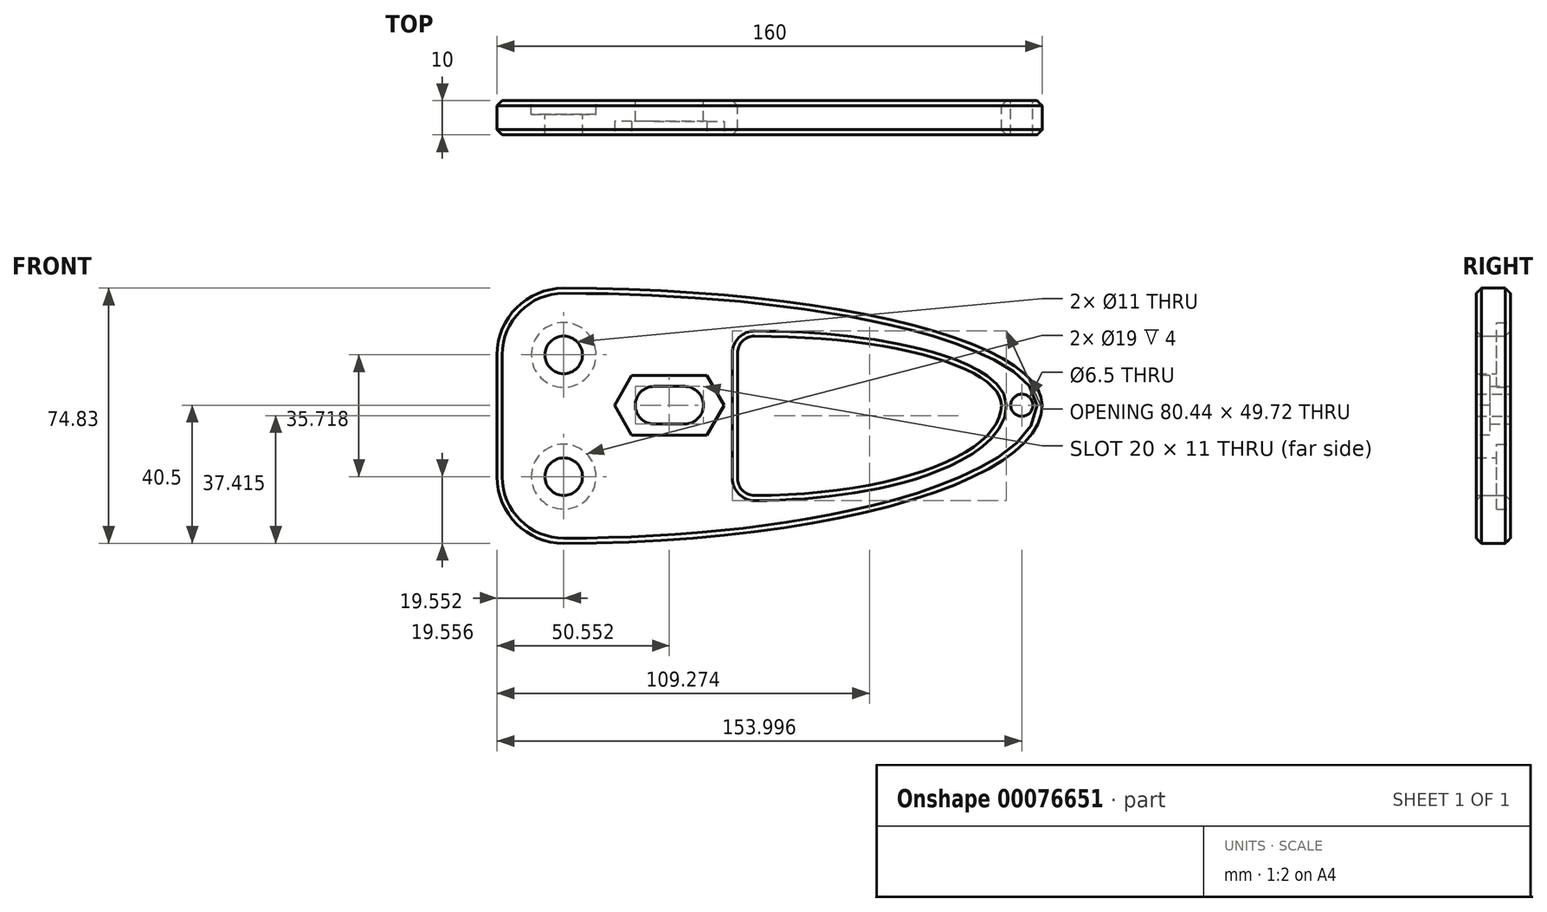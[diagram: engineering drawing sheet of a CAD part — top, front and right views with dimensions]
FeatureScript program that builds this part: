
annotation { "Feature Type Name" : "Feature", "Feature Type Description" : "" }
export const myFeature = defineFeature(function(context is Context, id is Id, definition is map)
    precondition{}
    {
        {
            var Q0;
            Q0=qCreatedBy(makeId("Front.planeOp"),FACE);
            var sketch = newSketch(context, id + "F0", { "sketchPlane" : qUnion([Q0])});
            skArc(sketch, "E0.filletArc", {"start": v(-61.04, 34.33) * mm, "mid": v(-74.87, 28.6) * mm, "end": v(-80.6, 14.77) * mm});
            skArc(sketch, "E1.filletArc", {"start": v(-80.6, -20.94) * mm, "mid": v(-74.87, -34.77) * mm, "end": v(-61.04, -40.5) * mm});
            skCircle(sketch, "E2", {"center": v(-61.04, -20.94) * mm, "radius": 5.5 * mm});
            skCircle(sketch, "E3", {"center": v(-61.04, 14.77) * mm, "radius": 5.5 * mm});
            skArc(sketch, "E4", {"start": v(-25.54, -5.5) * mm, "mid": v(-20.04, 0) * mm, "end": v(-25.54, 5.5) * mm});
            skPoint(sketch, "E5.center.orphan", {"position": v(-61.04, 0) * mm});
            skPoint(sketch, "E6", {"position": v(-80.6, 0) * mm});
            skPoint(sketch, "E7", {"position": v(-10.04, 0) * mm});
            skPoint(sketch, "E8", {"position": v(79.4, 0) * mm});
            skPoint(sketch, "E9", {"position": v(-20.04, 0) * mm});
            skArc(sketch, "E10", {"start": v(-34.54, 5.5) * mm, "mid": v(-40.04, 0) * mm, "end": v(-34.54, -5.5) * mm});
            skLineSegment(sketch, "E11", {"start": v(-34.54, 5.5) * mm, "end": v(-25.54, 5.5) * mm});
            skLineSegment(sketch, "E12", {"start": v(-34.54, -5.5) * mm, "end": v(-25.54, -5.5) * mm});
            skEllipticalArc(sketch, "E13", {});
            skEllipticalArc(sketch, "E14.trimOffspring", {});
            skLineSegment(sketch, "E15", {"start": v(79.4, 0) * mm, "end": v(67.4, 0) * mm});
            skEllipticalArc(sketch, "E16", {});
            skEllipticalArc(sketch, "E17.trimOffspring", {});
            skLineSegment(sketch, "E18", {"start": v(-5.04, 20.27) * mm, "end": v(-5.04, 20.27) * mm});
            skLineSegment(sketch, "E19", {"start": v(-10.04, 15.27) * mm, "end": v(-10.04, 0) * mm});
            skLineSegment(sketch, "E20", {"start": v(-10.04, 0) * mm, "end": v(-10.04, -21.44) * mm});
            skLineSegment(sketch, "E21", {"start": v(-5.04, -26.44) * mm, "end": v(-5.04, -26.44) * mm});
            skPoint(sketch, "E22.start.orphan", {"position": v(-61.04, 20.27) * mm});
            skPoint(sketch, "E23.start.orphan", {"position": v(-61.04, -26.44) * mm});
            skLineSegment(sketch, "E24", {"start": v(-80.6, 14.77) * mm, "end": v(-80.6, -20.94) * mm});
            skPoint(sketch, "E25.visualSharp", {"position": v(-10.04, 20.27) * mm});
            skArc(sketch, "E25.filletArc", {"start": v(-5.04, 20.27) * mm, "mid": v(-8.57, 18.8) * mm, "end": v(-10.04, 15.27) * mm});
            skPoint(sketch, "E26.visualSharp", {"position": v(-10.04, -26.44) * mm});
            skArc(sketch, "E26.filletArc", {"start": v(-10.04, -21.44) * mm, "mid": v(-8.57, -24.98) * mm, "end": v(-5.04, -26.44) * mm});
            skCircle(sketch, "E27", {"center": v(73.4, 0) * mm, "radius": 3.25 * mm});
            skCircle(sketch, "E28", {"center": v(-61.04, 14.77) * mm, "radius": 9.5 * mm});
            skCircle(sketch, "E29", {"center": v(-61.04, -20.94) * mm, "radius": 9.5 * mm});
            const initialGuessF0  = {"E13": [-0.061037882258116044, 0, 0, -1, 0.0405, 0.140444, 6.283185307179586, 1.5707963267948966], "E14.trimOffspring": [-0.061037882258116044, 0, 0, 1, 0.03433, 0.140444, 4.71238898038469, 6.283185307179586], "E16": [-0.005037882258116042, 0, 0, 1, 0.020274, 0.072444, 4.71238898038469, 6.283185307179586], "E17.trimOffspring": [-0.005037882258116042, 0, 0, -1, 0.026444, 0.072444, 6.283185307179586, 1.5707963267948966]};
            skSetInitialGuess(sketch, initialGuessF0);
            skSolve(sketch);
        }
        {
            var Q0;
            Q0 = qSketchRegion(id + "F0", true);
            var Q1;
            Q1=makeQuery(id+"F0.imprint","IMPRINT",FACE,{"disambiguationData":[TD([[makeQuery(id+"F0.imprint","IMPRINT",EDGE,{"derivedFrom":sQuery(id+"F0.wireOp",EDGE,"E3")}),-1.0]])]});
            var Q2;
            Q2=makeQuery(id+"F0.imprint","IMPRINT",FACE,{"disambiguationData":[TD([[makeQuery(id+"F0.imprint","IMPRINT",EDGE,{"derivedFrom":sQuery(id+"F0.wireOp",EDGE,"E2")}),-1.0]])]});
            extrude(context, id + "F1", {"entities" : qUnion([Q0, Q1, Q2]), "depth" : 10 * mm});
        }
        {
            var Q0;
            Q0=makeQuery(id+"F0.imprint","IMPRINT",FACE,{"disambiguationData":[TD([[makeQuery(id+"F0.imprint","IMPRINT",EDGE,{"derivedFrom":sQuery(id+"F0.wireOp",EDGE,"E3")}),-1.0]])]});
            var Q1;
            Q1=makeQuery(id+"F0.imprint","IMPRINT",FACE,{"disambiguationData":[TD([[makeQuery(id+"F0.imprint","IMPRINT",EDGE,{"derivedFrom":sQuery(id+"F0.wireOp",EDGE,"E2")}),-1.0]])]});
            extrude(context, id + "F2", {"entities" : qUnion([Q0, Q1]), "operationType" : NewBodyOperationType.REMOVE, "depth" : 4 * mm});
        }
        {
            var Q0;
            Q0=makeQuery(id+"F1.opExtrude","CAP_FACE",FACE,{"disambiguationData":[OSD([sQuery(id+"F0.wireOp",EDGE,"E0.filletArc"),sQuery(id+"F0.wireOp",EDGE,"E1.filletArc"),sQuery(id+"F0.wireOp",EDGE,"E2"),sQuery(id+"F0.wireOp",EDGE,"E3"),sQuery(id+"F0.wireOp",EDGE,"E4"),sQuery(id+"F0.wireOp",EDGE,"E10"),sQuery(id+"F0.wireOp",EDGE,"E11"),sQuery(id+"F0.wireOp",EDGE,"E12"),sQuery(id+"F0.wireOp",EDGE,"E13"),sQuery(id+"F0.wireOp",EDGE,"E14.trimOffspring"),sQuery(id+"F0.wireOp",EDGE,"E16"),sQuery(id+"F0.wireOp",EDGE,"E17.trimOffspring"),sQuery(id+"F0.wireOp",EDGE,"E19"),sQuery(id+"F0.wireOp",EDGE,"E20"),sQuery(id+"F0.wireOp",EDGE,"E24"),sQuery(id+"F0.wireOp",EDGE,"E25.filletArc"),sQuery(id+"F0.wireOp",EDGE,"E26.filletArc"),sQuery(id+"F0.wireOp",EDGE,"E27")])],"isStart":false});
            var sketch = newSketch(context, id + "F3", { "sketchPlane" : qUnion([Q0])});
            skPoint(sketch, "E30", {"position": v(-20.04, 0) * mm});
            skPoint(sketch, "E31", {"position": v(-29.04, 0) * mm});
            skLineSegment(sketch, "E32.1", {"start": v(-18.99, 8.75) * mm, "end": v(-13.93, 0) * mm});
            skLineSegment(sketch, "E32.2", {"start": v(-13.93, 0) * mm, "end": v(-18.99, -8.75) * mm});
            skLineSegment(sketch, "E33", {"start": v(-18.99, 8.75) * mm, "end": v(-41.09, 8.75) * mm});
            skLineSegment(sketch, "E34", {"start": v(-41.09, -8.75) * mm, "end": v(-18.99, -8.75) * mm});
            skPoint(sketch, "E35", {"position": v(-40.04, 0) * mm});
            skPoint(sketch, "E36", {"position": v(-31.04, 0) * mm});
            skLineSegment(sketch, "E37", {"start": v(-40.04, 0) * mm, "end": v(-20.04, 0) * mm});
            skLineSegment(sketch, "E38", {"start": v(-30.04, 0) * mm, "end": v(-30.04, 8.75) * mm, "construction": true});
            skLineSegment(sketch, "E39.MirrorCS", {"start": v(-41.09, 8.75) * mm, "end": v(-46.14, 0) * mm});
            skLineSegment(sketch, "E40.MirrorCS", {"start": v(-46.14, 0) * mm, "end": v(-41.09, -8.75) * mm});
            skSolve(sketch);
        }
        {
            var Q0;
            Q0 = qSketchRegion(id + "F3", true);
            extrude(context, id + "F4", {"entities" : qUnion([Q0]), "operationType" : NewBodyOperationType.REMOVE, "oppositeDirection" : true, "depth" : 4 * mm});
        }
        {
            var Q0;
            Q0=makeQuery(id+"F1.opExtrude","CAP_EDGE",EDGE,{"disambiguationData":[OSD([sQuery(id+"F0.wireOp",EDGE,"E14.trimOffspring")])],"isStart":false});
            var Q1;
            Q1=makeQuery(id+"F1.opExtrude","CAP_EDGE",EDGE,{"disambiguationData":[OSD([sQuery(id+"F0.wireOp",EDGE,"E19"),sQuery(id+"F0.wireOp",EDGE,"E20")])],"isStart":false});
            var Q2;
            Q2=makeQuery(id+"F1.opExtrude","CAP_EDGE",EDGE,{"disambiguationData":[OSD([sQuery(id+"F0.wireOp",EDGE,"E19"),sQuery(id+"F0.wireOp",EDGE,"E20")])],"isStart":true});
            var Q3;
            Q3=makeQuery(id+"F1.opExtrude","CAP_EDGE",EDGE,{"disambiguationData":[OSD([sQuery(id+"F0.wireOp",EDGE,"E14.trimOffspring")])],"isStart":true});
            chamfer(context, id + "F5", {"entities" : qUnion([Q0, Q1, Q2, Q3]), "width" : 1.5 * mm, "tangentPropagation" : true});
        }
    });
